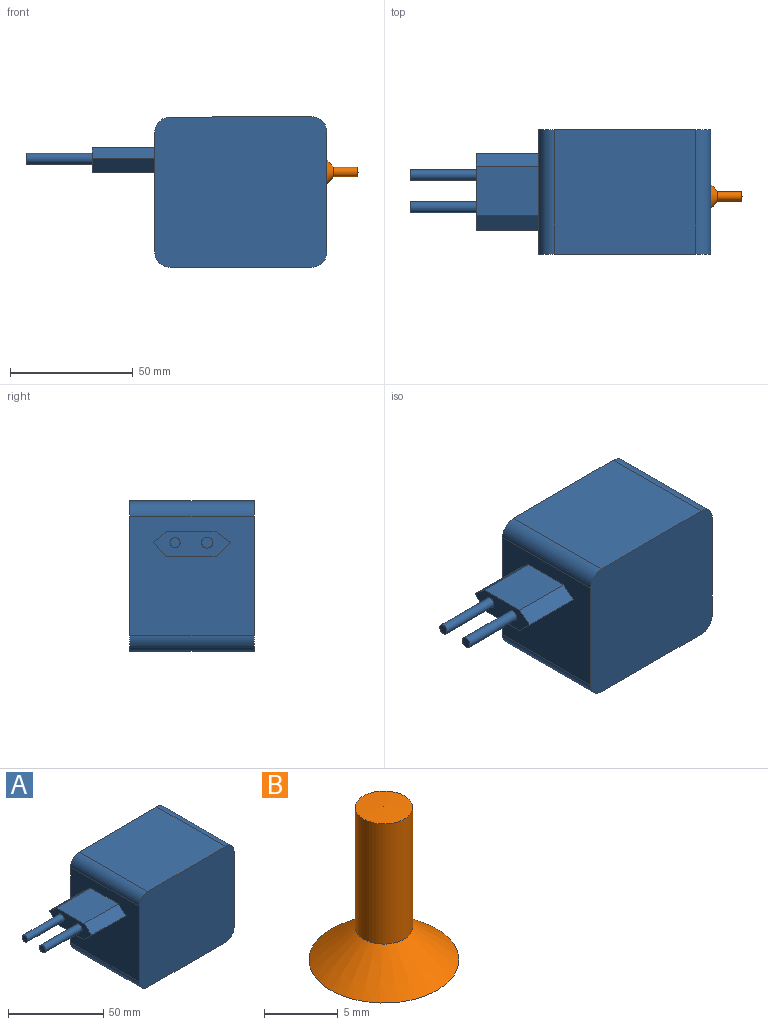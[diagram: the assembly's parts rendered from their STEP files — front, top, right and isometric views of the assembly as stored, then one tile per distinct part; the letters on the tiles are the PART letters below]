
ASSEMBLY  parts=2 mates=1
PART A: 23 faces, bbox 122.8x50.8x61.6 mm
  f0: cylinder r=6.35mm len=50.8mm, axis (0,1,0), area 506.7mm2, adj f1,f7,f8,f9
  f1: plane 50.8x48.87mm, normal (1,0,0), area 2462.1mm2, adj f0,f2,f8,f9,f21
  f2: cylinder r=6.35mm len=50.8mm, axis (0,1,0), area 508.1mm2, adj f1,f3,f8,f9
  f3: plane 57.56x50.8mm, normal (0,0,1), area 2924.1mm2, adj f2,f4,f8,f9
  f4: cylinder r=6.35mm len=50.8mm, axis (0,1,0), area 505.3mm2, adj f3,f5,f8,f9
  f5: plane 50.8x48.61mm, normal (-1,0,0), area 2206.1mm2, adj f4,f6,f8,f9,f10,f11,f12,f13
  f6: cylinder r=6.35mm len=50.8mm, axis (0,1,0), area 506.7mm2, adj f5,f7,f8,f9
  f7: plane 57.56x50.8mm, normal (0,0,-1), area 2924.1mm2, adj f0,f6,f8,f9
  f8: plane 70.26x61.57mm, normal (0,-1,0), area 4282.1mm2, adj f0,f1,f2,f3,f4,f5,f6,f7
  f9: plane 70.26x61.57mm, normal (0,1,0), area 4282.1mm2, adj f0,f1,f2,f3,f4,f5,f6,f7
  f10: plane 25.4x20.33mm, normal (0,0,-1), area 516.5mm2, adj f5,f11,f15,f16
  f11: plane 25.4x5.9mm, normal (0,-0.7,-0.72), area 209.1mm2, adj f5,f10,f12,f16
  f12: plane 25.4x5.9mm, normal (0,-0.6,0.8), area 187.4mm2, adj f5,f11,f13,f16
  f13: plane 25.4x20.33mm, normal (0,0,1), area 516.5mm2, adj f5,f12,f14,f16
  f14: plane 25.4x5.25mm, normal (0,0.64,0.76), area 174.4mm2, adj f5,f13,f15,f16
  f15: plane 25.4x5.74mm, normal (0,0.74,-0.67), area 197.5mm2, adj f5,f10,f14,f16
  f16: plane 31.48x10.17mm, normal (-1,0,0), area 234.2mm2, adj f10,f11,f12,f13,f14,f15,f17,f19
  f17: cylinder r=2.07mm len=27.11mm, axis (1,0,0), area 353.3mm2, adj f16,f18
  f18: plane 4.15x4.15mm, normal (-1,0,0), area 13.5mm2, adj f17
  f19: cylinder r=2.23mm len=27.11mm, axis (1,0,0), area 379.9mm2, adj f16,f20
  f20: plane 4.46x4.46mm, normal (-1,0,0), area 15.6mm2, adj f19
  f21: cylinder r=2.54mm len=7.1mm, axis (1,0,0), area 113.4mm2, adj f1,f22
  f22: plane 5.08x5.08mm, normal (1,0,0), area 20.3mm2, adj f21
PART B: 4 faces, bbox 10.2x10.2x12.7 mm
  f0: cone r=0mm half-angle=88deg, axis (0,0,-1), area 11.8mm2, adj f3
  f1: plane 10.16x10.16mm, normal (0,0,-1), area 81.1mm2, adj f2
  f2: cone r=1.94mm half-angle=49.6deg, axis (0,0,-1), area 90.9mm2, adj f1,f3
  f3: cylinder r=1.94mm len=9.96mm, axis (0,0,-1), area 121.2mm2, adj f0,f2
PLACE A t=(-33.03,-3.87,-1.31)mm
PLACE B rot(axis=(0.71,0,0.71),180deg) t=(-25.19,-31.05,-5.03)mm
MATE pin_slot B.f0 <-> A.f21  axis (-1,0,0) through (-2.85,-31.05,14.56)mm
